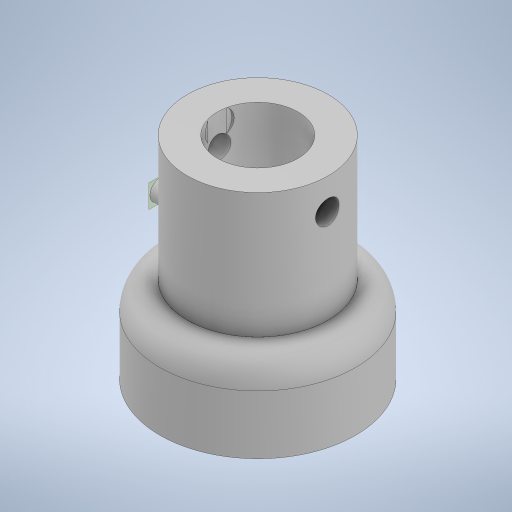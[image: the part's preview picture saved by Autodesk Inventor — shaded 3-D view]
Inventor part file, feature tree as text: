
AUTODESK INVENTOR PART (.ipt)
format: ipt  version: 2023 (Build 270158030, 158C)  size: 491,520 bytes
history: mixed  units: in
note: dims shown in document units (in); Inventor stores cm internally (conversion verified against a paired STEP export)
features: other x6, plane x1, extrude x1, sketch x1, imported_body x1
ambient origin geometry x8: Origin, YZ Plane, XZ Plane, XY Plane, X Axis, Y Axis, Z Axis, Center Point
bodies: Solid1 (imported_parasolid), Solid4 (imported_parasolid), Solid6 (imported_parasolid), Solid10 (imported_parasolid), Solid23 (imported_parasolid), Solid37 (imported_parasolid)
feature tree (10):
  other  "MouseEarbar"
  plane  "Work Plane1"
  extrude  "Extrusion1"  Depth=0.1181in
  sketch  "Sketch1"  dims[d0=0.0in d1=0.1181in d2=0.1575in d3=0.0in d4=0.0in]
  other  "Rat_ToothHolder"
  other  "Mouse_ToothHolder"
  other  "MouseNoseCone"
  other  "RatNoseCone"
  other  "RatEarbar_1"
  imported_body  NMx_Import_Brep_tag  [imported B-rep: ~5 faces, bbox_mm=None]
